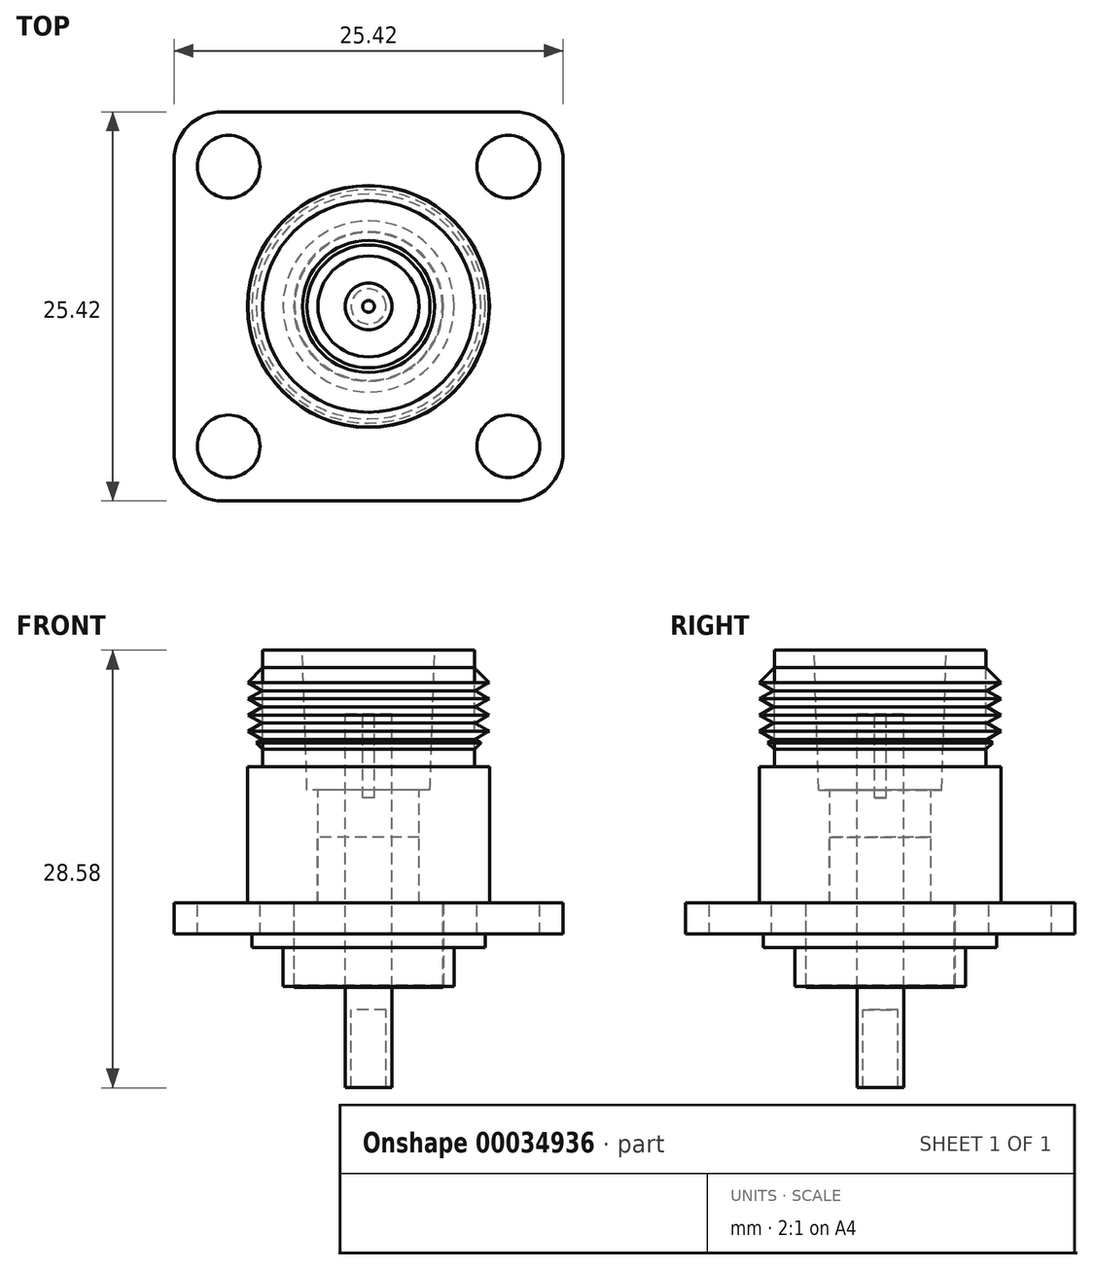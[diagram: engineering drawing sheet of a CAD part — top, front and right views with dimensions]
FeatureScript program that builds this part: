
annotation { "Feature Type Name" : "Feature", "Feature Type Description" : "" }
export const myFeature = defineFeature(function(context is Context, id is Id, definition is map)
    precondition{}
    {
        {
            var Q0;
            Q0=qCreatedBy(makeId("Top.planeOp"),FACE);
            var sketch = newSketch(context, id + "F0", { "sketchPlane" : qUnion([Q0])});
            skLineSegment(sketch, "E0", {"start": v(-32.66, 0) * mm, "end": v(40.56, 0) * mm, "construction": true});
            skLineSegment(sketch, "E1", {"start": v(0, 23.26) * mm, "end": v(0, -23.07) * mm, "construction": true});
            skLineSegment(sketch, "E2.rect.bottom", {"start": v(9.54, 12.71) * mm, "end": v(-9.54, 12.71) * mm});
            skLineSegment(sketch, "E2.rect.top", {"start": v(9.54, -12.71) * mm, "end": v(-9.54, -12.71) * mm});
            skLineSegment(sketch, "E2.rect.left", {"start": v(12.71, 9.54) * mm, "end": v(12.71, -9.54) * mm});
            skLineSegment(sketch, "E2.rect.right", {"start": v(-12.71, 9.54) * mm, "end": v(-12.71, -9.54) * mm});
            skPoint(sketch, "E2.rect.middle", {"position": v(0, 0) * mm});
            skCircle(sketch, "E3", {"center": v(9.13, 9.13) * mm, "radius": 2.05 * mm});
            skCircle(sketch, "E4.0.MirrorC", {"center": v(-9.13, 9.13) * mm, "radius": 2.05 * mm});
            skCircle(sketch, "E5.0.MirrorC", {"center": v(9.13, -9.13) * mm, "radius": 2.05 * mm});
            skCircle(sketch, "E6.0.MirrorC", {"center": v(-9.13, -9.13) * mm, "radius": 2.05 * mm});
            skPoint(sketch, "E7.visualSharp", {"position": v(-12.71, 12.71) * mm});
            skArc(sketch, "E7.filletArc", {"start": v(-9.54, 12.71) * mm, "mid": v(-11.78, 11.78) * mm, "end": v(-12.71, 9.54) * mm});
            skPoint(sketch, "E8.0.MirrorP", {"position": v(12.71, 12.71) * mm});
            skArc(sketch, "E9.filletArc", {"start": v(12.71, 9.54) * mm, "mid": v(11.78, 11.78) * mm, "end": v(9.54, 12.71) * mm});
            skPoint(sketch, "E10.visualSharp", {"position": v(12.71, -12.71) * mm});
            skArc(sketch, "E10.filletArc", {"start": v(9.54, -12.71) * mm, "mid": v(11.78, -11.78) * mm, "end": v(12.71, -9.54) * mm});
            skPoint(sketch, "E11.visualSharp", {"position": v(-12.71, -12.71) * mm});
            skArc(sketch, "E11.filletArc", {"start": v(-12.71, -9.54) * mm, "mid": v(-11.78, -11.78) * mm, "end": v(-9.54, -12.71) * mm});
            skSolve(sketch);
        }
        {
            var Q0;
            Q0=qSketchRegion(id+"F0",true);
            var Q1;
            Q1=qSketchRegion(id+"F2",true);
            extrude(context, id + "F1", {"entities" : qUnion([Q0, Q1]), "oppositeDirection" : true, "depth" : 2.03 * mm});
        }
        {
            var Q0;
            Q0=qCreatedBy(makeId("Right.planeOp"),FACE);
            var sketch = newSketch(context, id + "F2", { "sketchPlane" : qUnion([Q0])});
            skLineSegment(sketch, "E12", {"start": v(0, 38.13) * mm, "end": v(0, -57.33) * mm, "construction": true});
            skLineSegment(sketch, "E13", {"start": v(7.62, 0) * mm, "end": v(7.62, -2.91) * mm});
            skLineSegment(sketch, "E14", {"start": v(7.62, -2.91) * mm, "end": v(5.59, -2.91) * mm});
            skLineSegment(sketch, "E15", {"start": v(5.59, -2.91) * mm, "end": v(5.59, -5.46) * mm});
            skLineSegment(sketch, "E16", {"start": v(5.59, -5.46) * mm, "end": v(4.83, -5.46) * mm});
            skLineSegment(sketch, "E17", {"start": v(4.83, -5.46) * mm, "end": v(4.83, 0) * mm});
            skLineSegment(sketch, "E18", {"start": v(4.83, 0) * mm, "end": v(7.62, 0) * mm});
            skSolve(sketch);
        }
        {
            var Q0;
            Q0=qSketchRegion(id+"F2",true);
            var Q1;
            Q1=sQuery(id+"F2.wireOp",EDGE,"E12");
            revolve(context, id + "F3", {"operationType" : NewBodyOperationType.ADD, "entities" : qUnion([Q0]), "axis" : qUnion([Q1]), "revolveType" : RevolveType.FULL});
        }
        {
            var Q0;
            Q0=qCreatedBy(makeId("Right.planeOp"),FACE);
            var sketch = newSketch(context, id + "F4", { "sketchPlane" : qUnion([Q0])});
            skLineSegment(sketch, "E19", {"start": v(0, 27.56) * mm, "end": v(0, -14.21) * mm, "construction": true});
            skLineSegment(sketch, "E20", {"start": v(7.9, 0) * mm, "end": v(7.9, 8.9) * mm});
            skLineSegment(sketch, "E21", {"start": v(7.9, 8.9) * mm, "end": v(6.9, 8.9) * mm});
            skLineSegment(sketch, "E22", {"start": v(6.9, 8.9) * mm, "end": v(6.9, 16.51) * mm});
            skLineSegment(sketch, "E23", {"start": v(6.9, 16.51) * mm, "end": v(4.32, 16.51) * mm});
            skLineSegment(sketch, "E24", {"start": v(4.32, 16.51) * mm, "end": v(4.01, 7.4) * mm});
            skLineSegment(sketch, "E25", {"start": v(4.01, 7.4) * mm, "end": v(3.3, 7.4) * mm});
            skLineSegment(sketch, "E26", {"start": v(3.3, 7.4) * mm, "end": v(3.3, 0) * mm});
            skLineSegment(sketch, "E27", {"start": v(3.3, 0) * mm, "end": v(7.9, 0) * mm});
            skSolve(sketch);
        }
        {
            var Q0;
            Q0=qSketchRegion(id+"F4",true);
            var Q1;
            Q1=sQuery(id+"F4.wireOp",EDGE,"E19");
            revolve(context, id + "F5", {"operationType" : NewBodyOperationType.ADD, "entities" : qUnion([Q0]), "axis" : qUnion([Q1]), "revolveType" : RevolveType.FULL});
        }
        {
            var Q0;
            Q0=qCreatedBy(makeId("Right.planeOp"),FACE);
            var sketch = newSketch(context, id + "F6", { "sketchPlane" : qUnion([Q0])});
            skLineSegment(sketch, "E28", {"start": v(0, 35.83) * mm, "end": v(0, -34.84) * mm, "construction": true});
            skLineSegment(sketch, "E29", {"start": v(4.88, 0) * mm, "end": v(4.88, -5.38) * mm});
            skLineSegment(sketch, "E30", {"start": v(4.88, -5.38) * mm, "end": v(0, -5.38) * mm});
            skLineSegment(sketch, "E31", {"start": v(0, -5.38) * mm, "end": v(0, 0) * mm});
            skLineSegment(sketch, "E32", {"start": v(0, 0) * mm, "end": v(4.88, 0) * mm});
            skSolve(sketch);
        }
        {
            var Q0;
            Q0=qSketchRegion(id+"F6",true);
            var Q1;
            Q1=sQuery(id+"F6.wireOp",EDGE,"E28");
            revolve(context, id + "F7", {"operationType" : NewBodyOperationType.REMOVE, "entities" : qUnion([Q0]), "axis" : qUnion([Q1]), "revolveType" : RevolveType.FULL, "oppositeDirection" : true});
        }
        {
            var Q0;
            Q0=qCreatedBy(makeId("Right.planeOp"),FACE);
            var sketch = newSketch(context, id + "F8", { "sketchPlane" : qUnion([Q0])});
            skLineSegment(sketch, "E33", {"start": v(0, 30.77) * mm, "end": v(0, -24.02) * mm});
            skLineSegment(sketch, "E34", {"start": v(4.85, 0) * mm, "end": v(4.85, -5.51) * mm});
            skLineSegment(sketch, "E35", {"start": v(4.85, -5.51) * mm, "end": v(0, -5.51) * mm});
            skLineSegment(sketch, "E36", {"start": v(0, -5.51) * mm, "end": v(0, 4.3) * mm});
            skLineSegment(sketch, "E37", {"start": v(0, 4.3) * mm, "end": v(3.32, 4.3) * mm});
            skLineSegment(sketch, "E38", {"start": v(3.32, 4.3) * mm, "end": v(3.32, 0) * mm});
            skLineSegment(sketch, "E39", {"start": v(3.32, 0) * mm, "end": v(4.85, 0) * mm});
            skSolve(sketch);
        }
        {
            var Q0;
            Q0=qSketchRegion(id+"F8",true);
            var Q1;
            Q1=sQuery(id+"F8.wireOp",EDGE,"E33");
            revolve(context, id + "F9", {"entities" : qUnion([Q0]), "axis" : qUnion([Q1]), "revolveType" : RevolveType.FULL});
        }
        {
            var Q0;
            Q0=qCreatedBy(makeId("Right.planeOp"),FACE);
            var sketch = newSketch(context, id + "F10", { "sketchPlane" : qUnion([Q0])});
            skLineSegment(sketch, "E40", {"start": v(0, 39.59) * mm, "end": v(0, -42.33) * mm, "construction": true});
            skLineSegment(sketch, "E41", {"start": v(0, 6.86) * mm, "end": v(0.38, 6.86) * mm});
            skLineSegment(sketch, "E42", {"start": v(0.38, 6.86) * mm, "end": v(0.38, 12.32) * mm});
            skLineSegment(sketch, "E43", {"start": v(0.38, 12.32) * mm, "end": v(1.52, 12.32) * mm});
            skLineSegment(sketch, "E44", {"start": v(1.52, 12.32) * mm, "end": v(1.52, -12.07) * mm});
            skLineSegment(sketch, "E45", {"start": v(1.52, -12.07) * mm, "end": v(1.14, -12.07) * mm});
            skLineSegment(sketch, "E46", {"start": v(1.14, -12.07) * mm, "end": v(1.14, -6.99) * mm});
            skLineSegment(sketch, "E47", {"start": v(1.14, -6.99) * mm, "end": v(0, -6.99) * mm});
            skLineSegment(sketch, "E48", {"start": v(0, 6.86) * mm, "end": v(0, -6.99) * mm});
            skSolve(sketch);
        }
        {
            var Q0;
            Q0=makeQuery(id+"F10.imprint","IMPRINT",FACE,{"disambiguationData":[TD([[makeQuery(id+"F10.imprint","IMPRINT",EDGE,{"derivedFrom":sQuery(id+"F10.wireOp",EDGE,"E41")}),-1.0]])]});
            var Q1;
            Q1=sQuery(id+"F10.wireOp",EDGE,"E40");
            revolve(context, id + "F11", {"entities" : qUnion([Q0]), "axis" : qUnion([Q1]), "revolveType" : RevolveType.FULL});
        }
        {
            var Q0;
            Q0=qCreatedBy(makeId("Right.planeOp"),FACE);
            var sketch = newSketch(context, id + "F12", { "sketchPlane" : qUnion([Q0])});
            skLineSegment(sketch, "E49", {"start": v(0, 18.76) * mm, "end": v(0, 5.5) * mm, "construction": true});
            skLineSegment(sketch, "E50", {"start": v(7.87, 17.2) * mm, "end": v(7.87, 9) * mm, "construction": true});
            skLineSegment(sketch, "E51", {"start": v(6.9, 18.19) * mm, "end": v(6.9, 6.96) * mm, "construction": true});
            skLineSegment(sketch, "E52", {"start": v(6.1, 15.37) * mm, "end": v(9.18, 15.37) * mm, "construction": true});
            skLineSegment(sketch, "E53", {"start": v(5.9, 10.03) * mm, "end": v(9.16, 10.03) * mm, "construction": true});
            skLineSegment(sketch, "E54", {"start": v(6.9, 15.37) * mm, "end": v(7.87, 14.4) * mm});
            skLineSegment(sketch, "E55", {"start": v(7.87, 14.4) * mm, "end": v(7.87, 10.17) * mm, "construction": true});
            skLineSegment(sketch, "E56", {"start": v(7.35, 10.47) * mm, "end": v(6.9, 10.03) * mm});
            skLineSegment(sketch, "E57", {"start": v(6.9, 10.03) * mm, "end": v(6.9, 15.37) * mm});
            skLineSegment(sketch, "E58", {"start": v(7.87, 14.4) * mm, "end": v(6.96, 13.87) * mm});
            skLineSegment(sketch, "E59", {"start": v(6.96, 13.87) * mm, "end": v(7.87, 13.34) * mm});
            skLineSegment(sketch, "E60.0.1.0", {"start": v(7.87, 13.34) * mm, "end": v(6.96, 12.81) * mm});
            skLineSegment(sketch, "E60.0.1.1", {"start": v(6.96, 12.81) * mm, "end": v(7.87, 12.29) * mm});
            skLineSegment(sketch, "E60.0.2.0", {"start": v(7.87, 12.29) * mm, "end": v(6.96, 11.76) * mm});
            skLineSegment(sketch, "E60.0.2.1", {"start": v(6.96, 11.76) * mm, "end": v(7.87, 11.23) * mm});
            skLineSegment(sketch, "E60.0.3.0", {"start": v(7.87, 11.23) * mm, "end": v(6.96, 10.7) * mm});
            skLineSegment(sketch, "E60.0.3.1", {"start": v(6.96, 10.7) * mm, "end": v(7.35, 10.47) * mm});
            skLineSegment(sketch, "E60.direction1", {"start": v(6.96, 13.87) * mm, "end": v(32.36, 13.87) * mm, "construction": true});
            skLineSegment(sketch, "E60.direction2", {"start": v(6.96, 13.87) * mm, "end": v(6.96, 12.81) * mm, "construction": true});
            skPoint(sketch, "E61.orphan", {"position": v(7.87, 10.17) * mm});
            skSolve(sketch);
        }
        {
            var Q0;
            Q0=makeQuery(id+"F12.imprint","IMPRINT",FACE,{"disambiguationData":[TD([[makeQuery(id+"F12.imprint","IMPRINT",EDGE,{"derivedFrom":sQuery(id+"F12.wireOp",EDGE,"E54")}),-1.0]])]});
            var Q1;
            Q1=sQuery(id+"F12.wireOp",EDGE,"E55");
            var Q2;
            Q2=sQuery(id+"F12.wireOp",EDGE,"E49");
            revolve(context, id + "F13", {"entities" : qUnion([Q0]), "surfaceEntities" : qUnion([Q1]), "axis" : qUnion([Q2]), "revolveType" : RevolveType.FULL});
        }
    });
